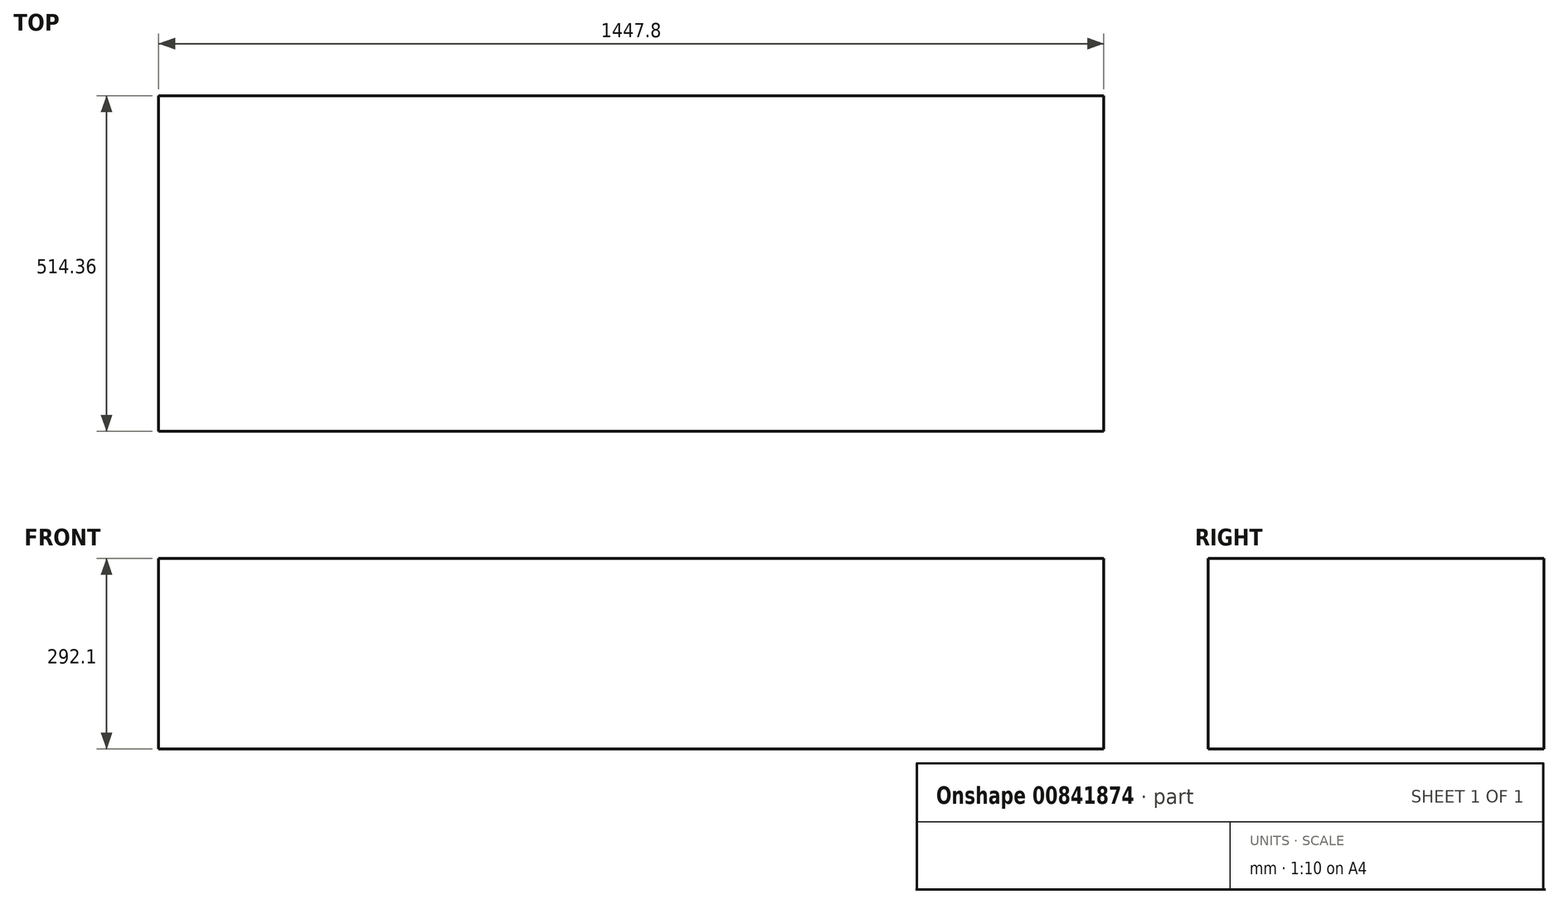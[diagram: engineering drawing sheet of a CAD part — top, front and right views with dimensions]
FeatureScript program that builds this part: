
annotation { "Feature Type Name" : "Feature", "Feature Type Description" : "" }
export const myFeature = defineFeature(function(context is Context, id is Id, definition is map)
    precondition{}
    {
        {
            var Q0;
            Q0=qCreatedBy(makeId("Top.planeOp"),FACE);
            var sketch = newSketch(context, id + "F0", { "sketchPlane" : qUnion([Q0])});
            skLineSegment(sketch, "E0.bottom", {"start": v(723.9, 257.18) * mm, "end": v(-723.9, 257.18) * mm});
            skLineSegment(sketch, "E0.top", {"start": v(723.9, -257.18) * mm, "end": v(-723.9, -257.18) * mm});
            skLineSegment(sketch, "E0.left", {"start": v(723.9, 257.18) * mm, "end": v(723.9, -257.18) * mm});
            skLineSegment(sketch, "E0.right", {"start": v(-723.9, 257.18) * mm, "end": v(-723.9, -257.18) * mm});
            skPoint(sketch, "E0.middle", {"position": v(0, 0) * mm});
            skSolve(sketch);
        }
        {
            var Q0;
            Q0 = qSketchRegion(id + "F0", true);
            extrude(context, id + "F1", {"entities" : qUnion([Q0]), "depth" : 292.1 * mm, "offsetDistance" : 25.4 * mm});
        }
    });
